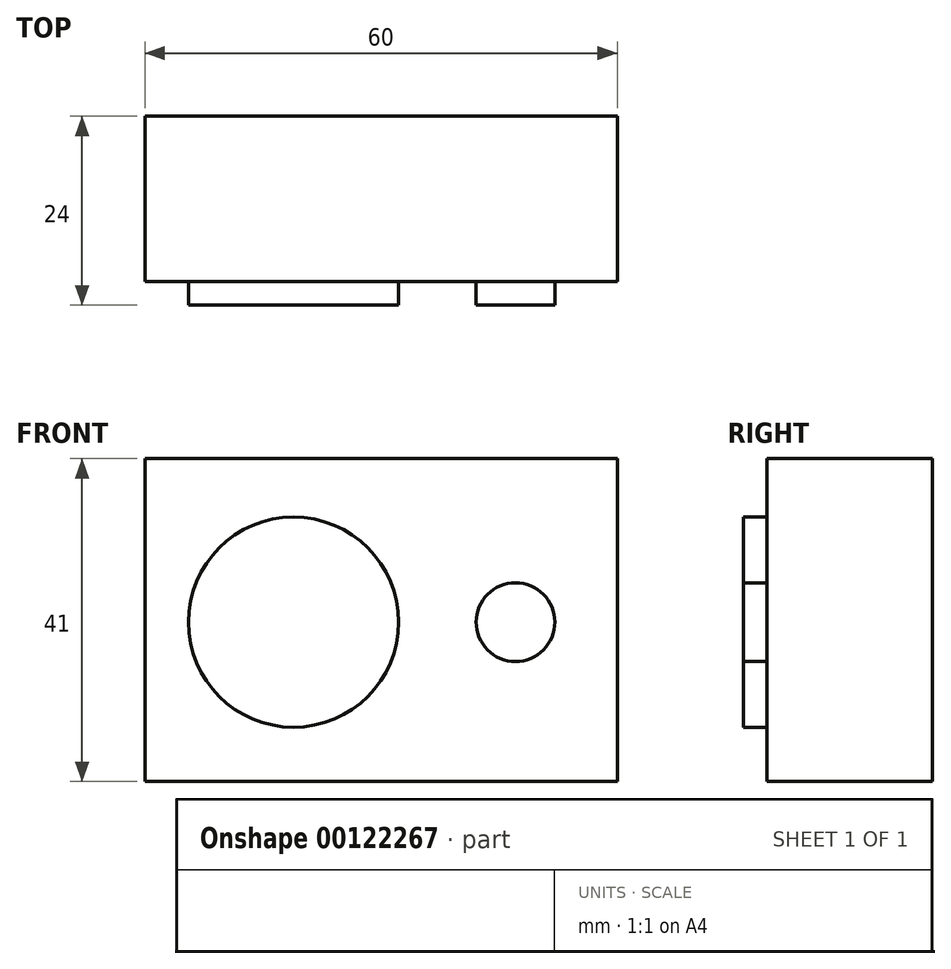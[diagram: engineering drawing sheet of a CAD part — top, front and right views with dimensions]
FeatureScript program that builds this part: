
annotation { "Feature Type Name" : "Feature", "Feature Type Description" : "" }
export const myFeature = defineFeature(function(context is Context, id is Id, definition is map)
    precondition{}
    {
        {
            var Q0;
            Q0=qCreatedBy(makeId("Front.planeOp"),FACE);
            var sketch = newSketch(context, id + "F0", { "sketchPlane" : qUnion([Q0])});
            skLineSegment(sketch, "E0.bottom", {"start": v(-30, 20.5) * mm, "end": v(30, 20.5) * mm});
            skLineSegment(sketch, "E0.top", {"start": v(-30, -20.5) * mm, "end": v(30, -20.5) * mm});
            skLineSegment(sketch, "E0.left", {"start": v(-30, 20.5) * mm, "end": v(-30, -20.5) * mm});
            skLineSegment(sketch, "E0.right", {"start": v(30, 20.5) * mm, "end": v(30, -20.5) * mm});
            skSolve(sketch);
        }
        {
            var Q0;
            Q0=makeQuery(id+"F0.imprint","IMPRINT",FACE,{"disambiguationData":[TD([[makeQuery(id+"F0.imprint","IMPRINT",EDGE,{"derivedFrom":sQuery(id+"F0.wireOp",EDGE,"E0.bottom")}),-1.0]])]});
            var Q1;
            Q1=makeQuery(id+"F0.imprint","IMPRINT",FACE,{"disambiguationData":[TD([[makeQuery(id+"F0.imprint","IMPRINT",EDGE,{"derivedFrom":sQuery(id+"F0.wireOp",EDGE,"EX49s7aD-b91A-ERHe-hLsK-9lN5zMDeHC7j")}),1.0]])]});
            var Q2;
            Q2=makeQuery(id+"F0.imprint","IMPRINT",FACE,{"disambiguationData":[TD([[makeQuery(id+"F0.imprint","IMPRINT",EDGE,{"derivedFrom":sQuery(id+"F0.wireOp",EDGE,"GADSJcvR-RPAu-Be0w-opZO-rJgRJN5l77oS")}),1.0]])]});
            extrude(context, id + "F1", {"entities" : qUnion([Q0, Q1, Q2]), "depth" : 21 * mm});
        }
        {
            var Q0;
            Q0=makeQuery(id+"F1.opExtrude","CAP_FACE",FACE,{"disambiguationData":[OSD([sQuery(id+"F0.wireOp",EDGE,"E0.bottom"),sQuery(id+"F0.wireOp",EDGE,"E0.top"),sQuery(id+"F0.wireOp",EDGE,"E0.left"),sQuery(id+"F0.wireOp",EDGE,"E0.right")])],"isStart":false});
            var sketch = newSketch(context, id + "F2", { "sketchPlane" : qUnion([Q0])});
            skCircle(sketch, "E1", {"center": v(-11.13, -0.28) * mm, "radius": 13.35 * mm});
            skCircle(sketch, "E2", {"center": v(17.07, -0.28) * mm, "radius": 5 * mm});
            skSolve(sketch);
        }
        {
            var Q0;
            Q0 = qSketchRegion(id + "F2", true);
            var Q1;
            Q1 = qConstructionFilter(qBodyType(qCreatedBy(id + "F2" ,EDGE), BodyType.WIRE), ConstructionObject.NO);
            extrude(context, id + "F3", {"entities" : qUnion([Q0]), "operationType" : NewBodyOperationType.ADD, "surfaceEntities" : qUnion([Q1]), "depth" : 3 * mm});
        }
    });
